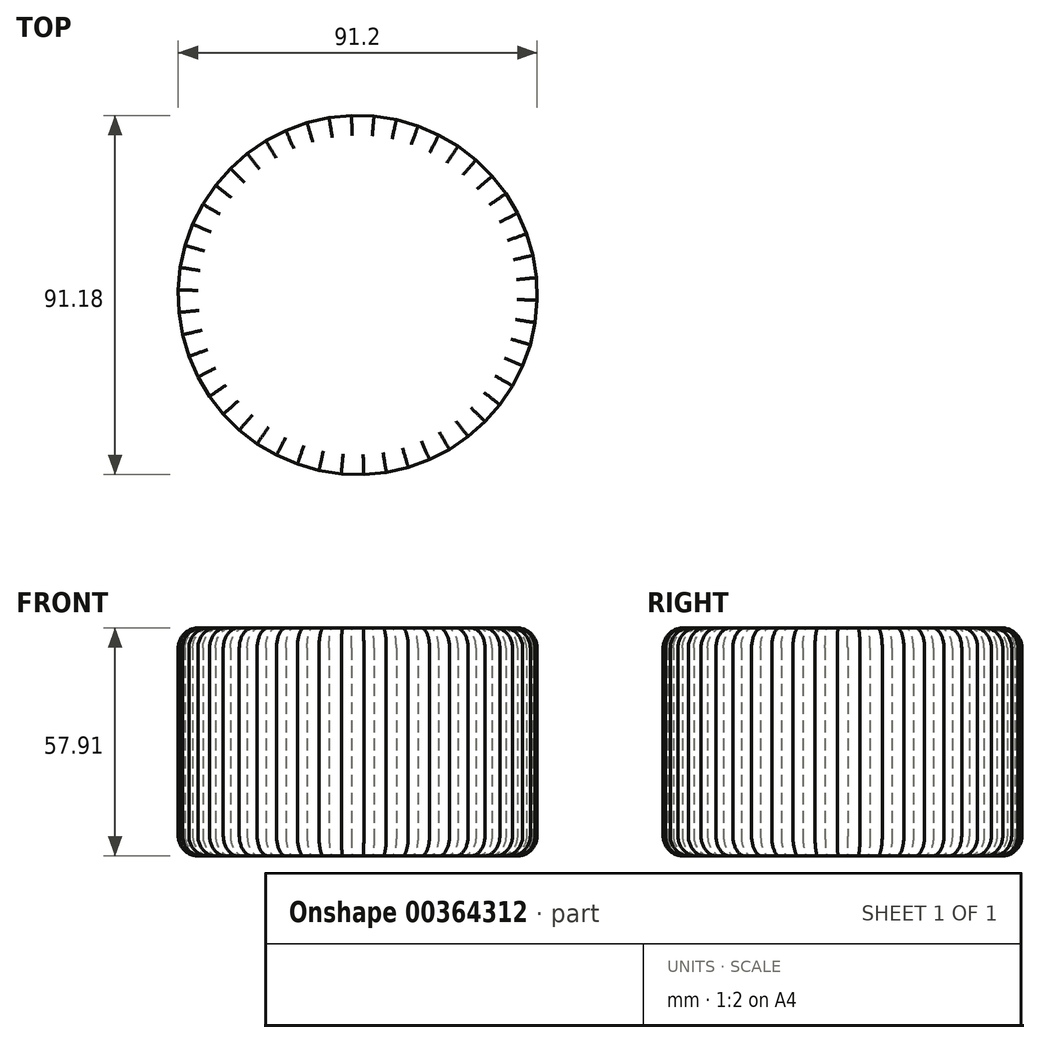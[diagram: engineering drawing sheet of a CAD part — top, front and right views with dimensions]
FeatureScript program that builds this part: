
annotation { "Feature Type Name" : "Feature", "Feature Type Description" : "" }
export const myFeature = defineFeature(function(context is Context, id is Id, definition is map)
    precondition{}
    {
        {
            var Q0;
            Q0=qCreatedBy(makeId("Top.planeOp"),FACE);
            var sketch = newSketch(context, id + "F0", { "sketchPlane" : qUnion([Q0])});
            skCircle(sketch, "E0.cCircle", {"center": v(92.33, 0) * mm, "radius": 45.53 * mm, "construction": true});
            skLineSegment(sketch, "E0.0", {"start": v(48.5, 12.6) * mm, "end": v(50.42, 18) * mm});
            skLineSegment(sketch, "E0.1", {"start": v(50.42, 18) * mm, "end": v(53, 23.1) * mm});
            skLineSegment(sketch, "E0.2", {"start": v(53, 23.1) * mm, "end": v(56.2, 27.86) * mm});
            skLineSegment(sketch, "E0.3", {"start": v(56.2, 27.86) * mm, "end": v(59.98, 32.16) * mm});
            skLineSegment(sketch, "E0.4", {"start": v(59.98, 32.16) * mm, "end": v(64.27, 35.96) * mm});
            skLineSegment(sketch, "E0.5", {"start": v(64.27, 35.96) * mm, "end": v(69, 39.2) * mm});
            skLineSegment(sketch, "E0.6", {"start": v(69, 39.2) * mm, "end": v(74.1, 41.81) * mm});
            skLineSegment(sketch, "E0.7", {"start": v(74.1, 41.81) * mm, "end": v(79.48, 43.77) * mm});
            skLineSegment(sketch, "E0.8", {"start": v(79.48, 43.77) * mm, "end": v(85.07, 45.03) * mm});
            skLineSegment(sketch, "E0.9", {"start": v(85.07, 45.03) * mm, "end": v(90.77, 45.59) * mm});
            skLineSegment(sketch, "E0.10", {"start": v(90.77, 45.59) * mm, "end": v(96.5, 45.43) * mm});
            skLineSegment(sketch, "E0.11", {"start": v(96.5, 45.43) * mm, "end": v(102.16, 44.55) * mm});
            skLineSegment(sketch, "E0.12", {"start": v(102.16, 44.55) * mm, "end": v(107.66, 42.96) * mm});
            skLineSegment(sketch, "E0.13", {"start": v(107.66, 42.96) * mm, "end": v(112.93, 40.7) * mm});
            skLineSegment(sketch, "E0.14", {"start": v(112.93, 40.7) * mm, "end": v(117.86, 37.8) * mm});
            skLineSegment(sketch, "E0.15", {"start": v(117.86, 37.8) * mm, "end": v(122.4, 34.3) * mm});
            skLineSegment(sketch, "E0.16", {"start": v(122.4, 34.3) * mm, "end": v(126.46, 30.26) * mm});
            skLineSegment(sketch, "E0.17", {"start": v(126.46, 30.26) * mm, "end": v(129.99, 25.75) * mm});
            skLineSegment(sketch, "E0.18", {"start": v(129.99, 25.75) * mm, "end": v(132.92, 20.82) * mm});
            skLineSegment(sketch, "E0.19", {"start": v(132.92, 20.82) * mm, "end": v(135.2, 15.57) * mm});
            skLineSegment(sketch, "E0.20", {"start": v(135.2, 15.57) * mm, "end": v(136.82, 10.08) * mm});
            skLineSegment(sketch, "E0.21", {"start": v(136.82, 10.08) * mm, "end": v(137.73, 4.42) * mm});
            skLineSegment(sketch, "E0.22", {"start": v(137.73, 4.42) * mm, "end": v(137.93, -1.3) * mm});
            skLineSegment(sketch, "E0.23", {"start": v(137.93, -1.3) * mm, "end": v(137.4, -7) * mm});
            skLineSegment(sketch, "E0.24", {"start": v(137.4, -7) * mm, "end": v(136.17, -12.6) * mm});
            skLineSegment(sketch, "E0.25", {"start": v(136.17, -12.6) * mm, "end": v(134.25, -18) * mm});
            skLineSegment(sketch, "E0.26", {"start": v(134.25, -18) * mm, "end": v(131.66, -23.1) * mm});
            skLineSegment(sketch, "E0.27", {"start": v(131.66, -23.1) * mm, "end": v(128.45, -27.86) * mm});
            skLineSegment(sketch, "E0.28", {"start": v(128.45, -27.86) * mm, "end": v(124.68, -32.16) * mm});
            skLineSegment(sketch, "E0.29", {"start": v(124.68, -32.16) * mm, "end": v(120.4, -35.96) * mm});
            skLineSegment(sketch, "E0.30", {"start": v(120.4, -35.96) * mm, "end": v(115.66, -39.2) * mm});
            skLineSegment(sketch, "E0.31", {"start": v(115.66, -39.2) * mm, "end": v(110.57, -41.81) * mm});
            skLineSegment(sketch, "E0.32", {"start": v(110.57, -41.81) * mm, "end": v(105.18, -43.77) * mm});
            skLineSegment(sketch, "E0.33", {"start": v(105.18, -43.77) * mm, "end": v(99.6, -45.03) * mm});
            skLineSegment(sketch, "E0.34", {"start": v(99.6, -45.03) * mm, "end": v(93.9, -45.59) * mm});
            skLineSegment(sketch, "E0.35", {"start": v(93.9, -45.59) * mm, "end": v(88.17, -45.43) * mm});
            skLineSegment(sketch, "E0.36", {"start": v(88.17, -45.43) * mm, "end": v(82.5, -44.55) * mm});
            skLineSegment(sketch, "E0.37", {"start": v(82.5, -44.55) * mm, "end": v(77, -42.96) * mm});
            skLineSegment(sketch, "E0.38", {"start": v(77, -42.96) * mm, "end": v(71.74, -40.7) * mm});
            skLineSegment(sketch, "E0.39", {"start": v(71.74, -40.7) * mm, "end": v(66.8, -37.8) * mm});
            skLineSegment(sketch, "E0.40", {"start": v(66.8, -37.8) * mm, "end": v(62.26, -34.3) * mm});
            skLineSegment(sketch, "E0.41", {"start": v(62.26, -34.3) * mm, "end": v(58.2, -30.26) * mm});
            skLineSegment(sketch, "E0.42", {"start": v(58.2, -30.26) * mm, "end": v(54.68, -25.75) * mm});
            skLineSegment(sketch, "E0.43", {"start": v(54.68, -25.75) * mm, "end": v(51.75, -20.82) * mm});
            skLineSegment(sketch, "E0.44", {"start": v(51.75, -20.82) * mm, "end": v(49.46, -15.57) * mm});
            skLineSegment(sketch, "E0.45", {"start": v(49.46, -15.57) * mm, "end": v(47.84, -10.08) * mm});
            skLineSegment(sketch, "E0.46", {"start": v(47.84, -10.08) * mm, "end": v(46.93, -4.42) * mm});
            skLineSegment(sketch, "E0.47", {"start": v(46.93, -4.42) * mm, "end": v(46.73, 1.3) * mm});
            skLineSegment(sketch, "E0.48", {"start": v(46.73, 1.3) * mm, "end": v(47.26, 7) * mm});
            skLineSegment(sketch, "E0.49", {"start": v(47.26, 7) * mm, "end": v(48.5, 12.6) * mm});
            skPoint(sketch, "E0.0.midPoint", {"position": v(49.45, 15.3) * mm});
            skSolve(sketch);
        }
        {
            var Q0;
            Q0=makeQuery(id+"F0.imprint","IMPRINT",FACE,{"disambiguationData":[TD([[makeQuery(id+"F0.imprint","IMPRINT",EDGE,{"derivedFrom":sQuery(id+"F0.wireOp",EDGE,"E0.0")}),-1.0]])]});
            extrude(context, id + "F1", {"entities" : qUnion([Q0]), "depth" : 57.9 * mm});
        }
        {
            var Q0;
            Q0=makeQuery(id+"F1.opExtrude","CAP_FACE",FACE,{"disambiguationData":[OSD([sQuery(id+"F0.wireOp",EDGE,"E0.0"),sQuery(id+"F0.wireOp",EDGE,"E0.1"),sQuery(id+"F0.wireOp",EDGE,"E0.2"),sQuery(id+"F0.wireOp",EDGE,"E0.3"),sQuery(id+"F0.wireOp",EDGE,"E0.4"),sQuery(id+"F0.wireOp",EDGE,"E0.5"),sQuery(id+"F0.wireOp",EDGE,"E0.6"),sQuery(id+"F0.wireOp",EDGE,"E0.7"),sQuery(id+"F0.wireOp",EDGE,"E0.8"),sQuery(id+"F0.wireOp",EDGE,"E0.9"),sQuery(id+"F0.wireOp",EDGE,"E0.10"),sQuery(id+"F0.wireOp",EDGE,"E0.11"),sQuery(id+"F0.wireOp",EDGE,"E0.12"),sQuery(id+"F0.wireOp",EDGE,"E0.13"),sQuery(id+"F0.wireOp",EDGE,"E0.14"),sQuery(id+"F0.wireOp",EDGE,"E0.15"),sQuery(id+"F0.wireOp",EDGE,"E0.16"),sQuery(id+"F0.wireOp",EDGE,"E0.17"),sQuery(id+"F0.wireOp",EDGE,"E0.18"),sQuery(id+"F0.wireOp",EDGE,"E0.19"),sQuery(id+"F0.wireOp",EDGE,"E0.20"),sQuery(id+"F0.wireOp",EDGE,"E0.21"),sQuery(id+"F0.wireOp",EDGE,"E0.22"),sQuery(id+"F0.wireOp",EDGE,"E0.23"),sQuery(id+"F0.wireOp",EDGE,"E0.24"),sQuery(id+"F0.wireOp",EDGE,"E0.25"),sQuery(id+"F0.wireOp",EDGE,"E0.26"),sQuery(id+"F0.wireOp",EDGE,"E0.27"),sQuery(id+"F0.wireOp",EDGE,"E0.28"),sQuery(id+"F0.wireOp",EDGE,"E0.29"),sQuery(id+"F0.wireOp",EDGE,"E0.30"),sQuery(id+"F0.wireOp",EDGE,"E0.31"),sQuery(id+"F0.wireOp",EDGE,"E0.32"),sQuery(id+"F0.wireOp",EDGE,"E0.33"),sQuery(id+"F0.wireOp",EDGE,"E0.34"),sQuery(id+"F0.wireOp",EDGE,"E0.35"),sQuery(id+"F0.wireOp",EDGE,"E0.36"),sQuery(id+"F0.wireOp",EDGE,"E0.37"),sQuery(id+"F0.wireOp",EDGE,"E0.38"),sQuery(id+"F0.wireOp",EDGE,"E0.39"),sQuery(id+"F0.wireOp",EDGE,"E0.40"),sQuery(id+"F0.wireOp",EDGE,"E0.41"),sQuery(id+"F0.wireOp",EDGE,"E0.42"),sQuery(id+"F0.wireOp",EDGE,"E0.43"),sQuery(id+"F0.wireOp",EDGE,"E0.44"),sQuery(id+"F0.wireOp",EDGE,"E0.45"),sQuery(id+"F0.wireOp",EDGE,"E0.46"),sQuery(id+"F0.wireOp",EDGE,"E0.47"),sQuery(id+"F0.wireOp",EDGE,"E0.48"),sQuery(id+"F0.wireOp",EDGE,"E0.49")])],"isStart":true});
            fillet(context, id + "F2", {"entities" : qUnion([Q0]), "radius" : 5.08 * mm, "tangentPropagation" : true, "allowEdgeOverflow" : false});
        }
        {
            var Q0;
            Q0=makeQuery(id+"F1.opExtrude","CAP_FACE",FACE,{"disambiguationData":[OSD([sQuery(id+"F0.wireOp",EDGE,"E0.0"),sQuery(id+"F0.wireOp",EDGE,"E0.1"),sQuery(id+"F0.wireOp",EDGE,"E0.2"),sQuery(id+"F0.wireOp",EDGE,"E0.3"),sQuery(id+"F0.wireOp",EDGE,"E0.4"),sQuery(id+"F0.wireOp",EDGE,"E0.5"),sQuery(id+"F0.wireOp",EDGE,"E0.6"),sQuery(id+"F0.wireOp",EDGE,"E0.7"),sQuery(id+"F0.wireOp",EDGE,"E0.8"),sQuery(id+"F0.wireOp",EDGE,"E0.9"),sQuery(id+"F0.wireOp",EDGE,"E0.10"),sQuery(id+"F0.wireOp",EDGE,"E0.11"),sQuery(id+"F0.wireOp",EDGE,"E0.12"),sQuery(id+"F0.wireOp",EDGE,"E0.13"),sQuery(id+"F0.wireOp",EDGE,"E0.14"),sQuery(id+"F0.wireOp",EDGE,"E0.15"),sQuery(id+"F0.wireOp",EDGE,"E0.16"),sQuery(id+"F0.wireOp",EDGE,"E0.17"),sQuery(id+"F0.wireOp",EDGE,"E0.18"),sQuery(id+"F0.wireOp",EDGE,"E0.19"),sQuery(id+"F0.wireOp",EDGE,"E0.20"),sQuery(id+"F0.wireOp",EDGE,"E0.21"),sQuery(id+"F0.wireOp",EDGE,"E0.22"),sQuery(id+"F0.wireOp",EDGE,"E0.23"),sQuery(id+"F0.wireOp",EDGE,"E0.24"),sQuery(id+"F0.wireOp",EDGE,"E0.25"),sQuery(id+"F0.wireOp",EDGE,"E0.26"),sQuery(id+"F0.wireOp",EDGE,"E0.27"),sQuery(id+"F0.wireOp",EDGE,"E0.28"),sQuery(id+"F0.wireOp",EDGE,"E0.29"),sQuery(id+"F0.wireOp",EDGE,"E0.30"),sQuery(id+"F0.wireOp",EDGE,"E0.31"),sQuery(id+"F0.wireOp",EDGE,"E0.32"),sQuery(id+"F0.wireOp",EDGE,"E0.33"),sQuery(id+"F0.wireOp",EDGE,"E0.34"),sQuery(id+"F0.wireOp",EDGE,"E0.35"),sQuery(id+"F0.wireOp",EDGE,"E0.36"),sQuery(id+"F0.wireOp",EDGE,"E0.37"),sQuery(id+"F0.wireOp",EDGE,"E0.38"),sQuery(id+"F0.wireOp",EDGE,"E0.39"),sQuery(id+"F0.wireOp",EDGE,"E0.40"),sQuery(id+"F0.wireOp",EDGE,"E0.41"),sQuery(id+"F0.wireOp",EDGE,"E0.42"),sQuery(id+"F0.wireOp",EDGE,"E0.43"),sQuery(id+"F0.wireOp",EDGE,"E0.44"),sQuery(id+"F0.wireOp",EDGE,"E0.45"),sQuery(id+"F0.wireOp",EDGE,"E0.46"),sQuery(id+"F0.wireOp",EDGE,"E0.47"),sQuery(id+"F0.wireOp",EDGE,"E0.48"),sQuery(id+"F0.wireOp",EDGE,"E0.49")])],"isStart":false});
            fillet(context, id + "F3", {"entities" : qUnion([Q0]), "radius" : 5.08 * mm, "tangentPropagation" : true, "allowEdgeOverflow" : false});
        }
    });
